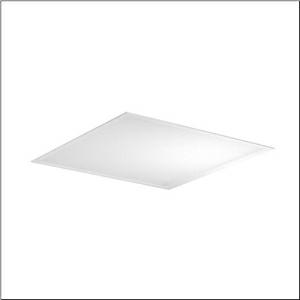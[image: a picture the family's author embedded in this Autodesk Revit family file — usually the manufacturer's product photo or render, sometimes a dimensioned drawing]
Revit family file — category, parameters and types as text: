
# Revit family: apollon_21_square_51mq12w72313
name_source: partatom
category: Lighting Fixtures
units: mm (PartAtom-declared; Revit-internal decimal feet)

## family parameters
Cut with Voids When Loaded = No
Host = Face
Light Source = No
Part Type = Normal
Room Calculation Point = No
Round Connector Dimension = Use Diameter
Shared = No

## types (1)
- Apollon 21 square (1 x LED, 4000 lm, 33 W, 3000K)
    Apparent Load = 33 VA
    CIE Flux Codes = 61 87 97 100 100
    Color Rendering = 80
    Color Temperature = 3000K
    Default Elevation = 1800 mm
    Description = Apollon 21 square, office luminaire, primary optical cover: micro prismatic cover, of PMMA, CAT 2 (L<= 3000cd/m²), light emission: direct distribution, primary light characteristic: symmetric, installation type: lay-in mounting, recessed, LED, rated luminous flux: 4.000lm, luminous efficacy: 121lm/W, light colour: 830, colour temperature: 3000K, control gear: ON/OFF, with terminal, 3-pole, mains connection: 220..240V, AC, 50/60Hz, rated input power: 33W, housing, of aluminium, traffic white (RAL 9016), module: M600, length: 596mm, width: 596mm, height: 40mm, housing upper side, of sheet steel, galvanised, protection rating (complete): IP20, protection rating (lamp compartment, on room side): IP50, insulation class (complete): insulation class II (safety insulation), certification: CE, ENEC, permissible operating ambient temperature: -20..+40°C, packaging unit: 1 piece
    Height = 0 mm  [stored 0 ft]
    Lamp = 1 x LED
    Lamp Light Flux = 4000 lm
    Lamp Power = 33 W
    Lamp count = 1
    Length = 595 mm
    Luminous efficacy = 121 lm/W
    Manufacturer = Siteco
    ModVariant = No
    Model = 51MQ12W72313
    Mounting Place = Ceiling
    Mounting Type = Recessed
    Number of Poles = 1
    OnlyDefault = Yes
    Power Factor = 1
    Product Name = Apollon 21 square
    Product group = office luminaire | ceiling recessed
    ProductGroupID = 400
    Protection Class = Protection class II
    Protection Degree = IP 20
    RLX_Detail_Level = 1
    RLX_Emergency_Light_Flux = 0 lm
    RLX_Emergency_Type = 0
    RLX_Emergency_Type_DB = No
    RlxData = <blob elided: 12445 chars, md5=938e2b4b>
    Socket = socket
    Standby Power = 0 W
    System Light Flux = 4000 lm
    System Power = 33 W
    Type Comments = Product without accessories
    Type Image = l_1291049.jpg
    URL = http://relux.com
    VarID = ---
    Voltage = 0 V
    Weight = 0.00 kg
    Width = 595 mm

note: [stored X ft] marks values corroborated as IEEE doubles in the binary element streams (Revit-internal decimal feet)

## geometry (parser evidence)
native form markers: Sweep x11
no freeform markers — native parametric forms only
